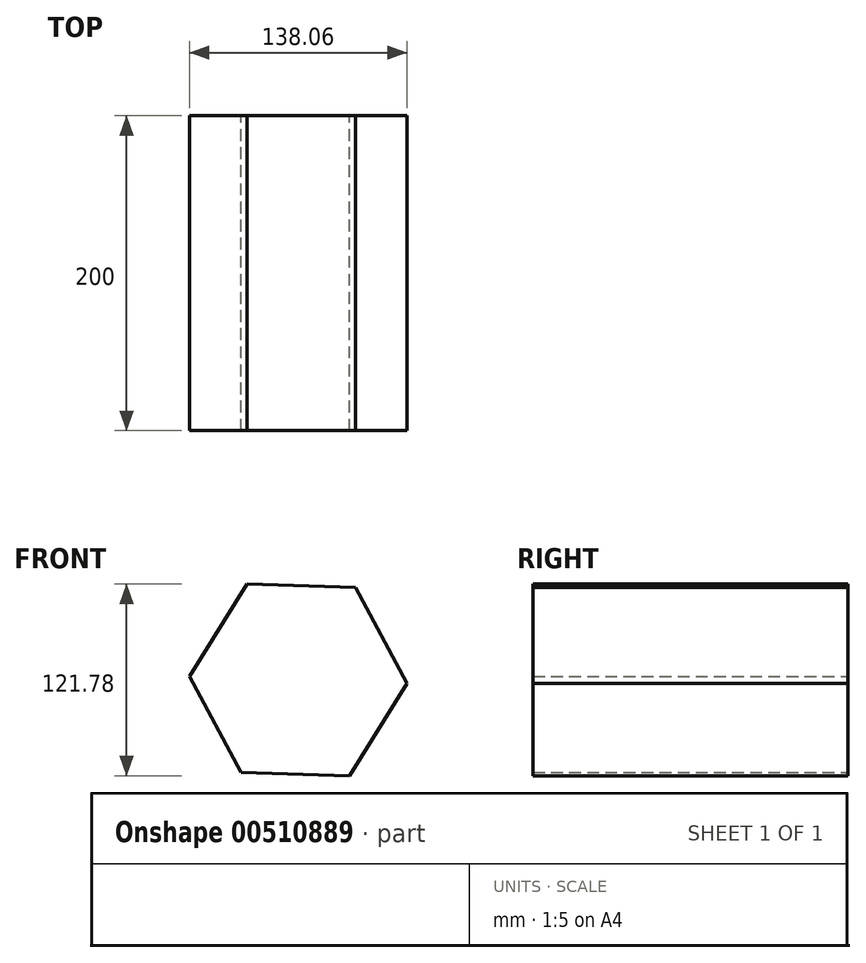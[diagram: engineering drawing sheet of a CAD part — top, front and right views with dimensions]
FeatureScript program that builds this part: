
annotation { "Feature Type Name" : "Feature", "Feature Type Description" : "" }
export const myFeature = defineFeature(function(context is Context, id is Id, definition is map)
    precondition{}
    {
        {
            var Q0;
            Q0=qCreatedBy(makeId("Front.planeOp"),FACE);
            var sketch = newSketch(context, id + "F0", { "sketchPlane" : qUnion([Q0])});
            skCircle(sketch, "E0.cCircle", {"center": v(0, 0) * mm, "radius": 69.06 * mm, "construction": true});
            skLineSegment(sketch, "E0.0", {"start": v(-36.43, -58.67) * mm, "end": v(-69.03, 2.22) * mm});
            skLineSegment(sketch, "E0.1", {"start": v(-69.03, 2.22) * mm, "end": v(-32.6, 60.89) * mm});
            skLineSegment(sketch, "E0.2", {"start": v(-32.6, 60.89) * mm, "end": v(36.43, 58.67) * mm});
            skLineSegment(sketch, "E0.3", {"start": v(36.43, 58.67) * mm, "end": v(69.03, -2.22) * mm});
            skLineSegment(sketch, "E0.4", {"start": v(69.03, -2.22) * mm, "end": v(32.6, -60.89) * mm});
            skLineSegment(sketch, "E0.5", {"start": v(32.6, -60.89) * mm, "end": v(-36.43, -58.67) * mm});
            skSolve(sketch);
        }
        {
            var Q0;
            Q0=qSketchRegion(id+"F0",true);
            extrude(context, id + "F1", {"entities" : qUnion([Q0]), "depth" : 200 * mm});
        }
    });
